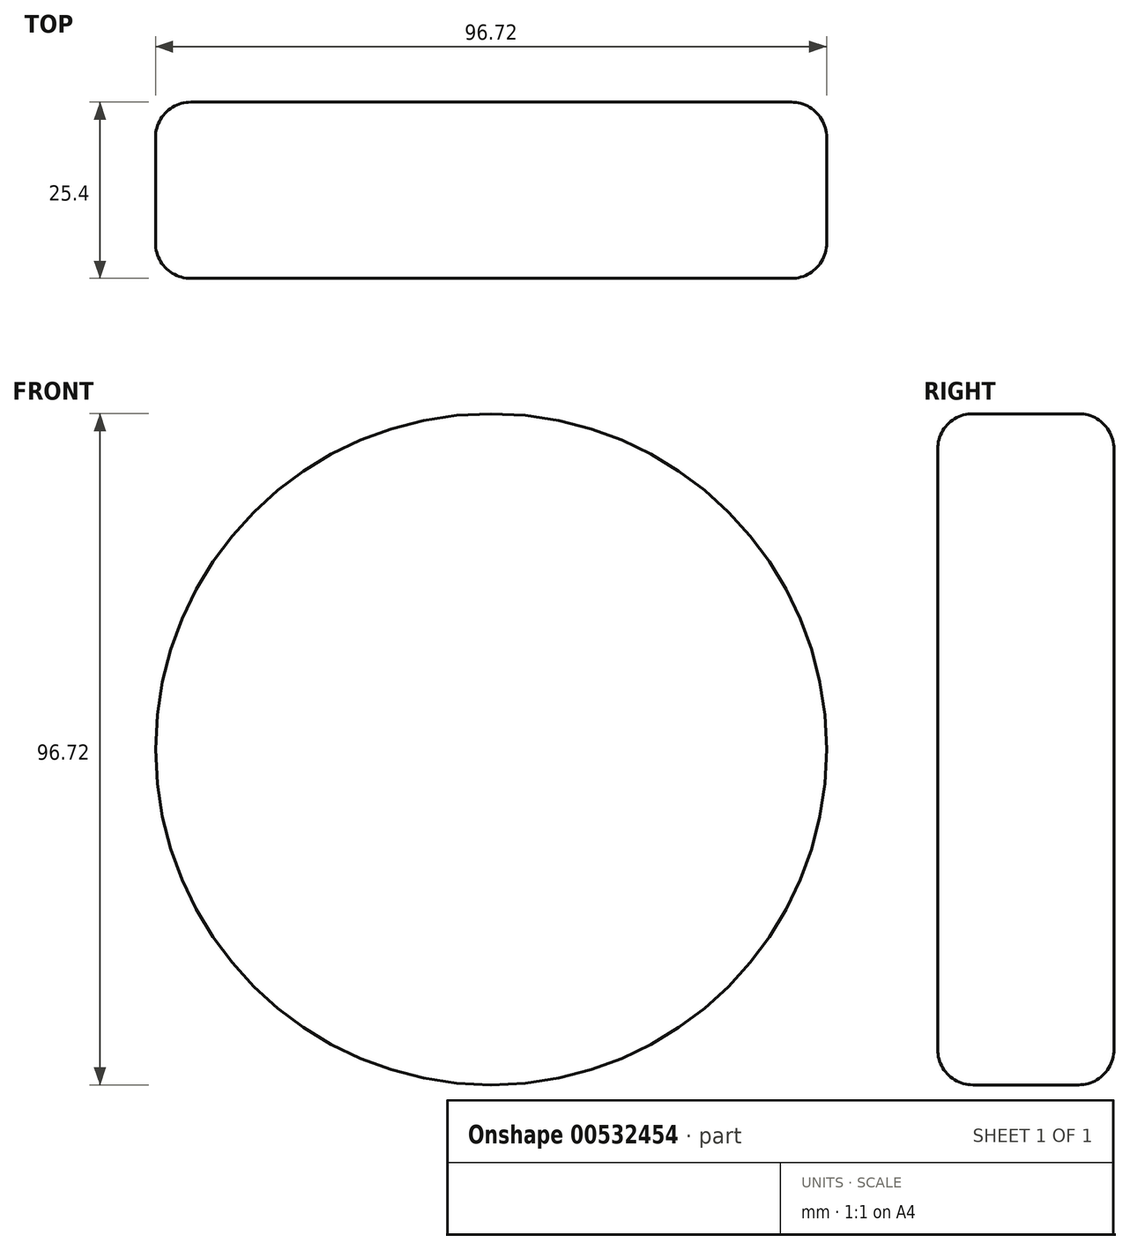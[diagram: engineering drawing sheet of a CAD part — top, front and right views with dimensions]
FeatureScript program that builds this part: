
annotation { "Feature Type Name" : "Feature", "Feature Type Description" : "" }
export const myFeature = defineFeature(function(context is Context, id is Id, definition is map)
    precondition{}
    {
        {
            var Q0;
            Q0=qCreatedBy(makeId("Front.planeOp"),FACE);
            var sketch = newSketch(context, id + "F0", { "sketchPlane" : qUnion([Q0])});
            skCircle(sketch, "E0", {"center": v(0, 0) * mm, "radius": 48.36 * mm});
            skSolve(sketch);
        }
        {
            var Q0;
            Q0=makeQuery(id+"F0.imprint","IMPRINT",FACE,{"disambiguationData":[TD([[makeQuery(id+"F0.imprint","IMPRINT",EDGE,{"derivedFrom":sQuery(id+"F0.wireOp",EDGE,"E0")}),1.0]])]});
            extrude(context, id + "F1", {"entities" : qUnion([Q0]), "depth" : 25.4 * mm, "offsetDistance" : 25.4 * mm});
        }
        {
            var Q0;
            Q0=makeQuery(id+"F1.opExtrude","CAP_EDGE",EDGE,{"disambiguationData":[OSD([sQuery(id+"F0.wireOp",EDGE,"E0")])],"isStart":false});
            var Q1;
            Q1=makeQuery(id+"F1.opExtrude","CAP_EDGE",EDGE,{"disambiguationData":[OSD([sQuery(id+"F0.wireOp",EDGE,"E0")])],"isStart":true});
            fillet(context, id + "F2", {"entities" : qUnion([Q0, Q1]), "radius" : 5.08 * mm, "tangentPropagation" : true, "allowEdgeOverflow" : false});
        }
    });
